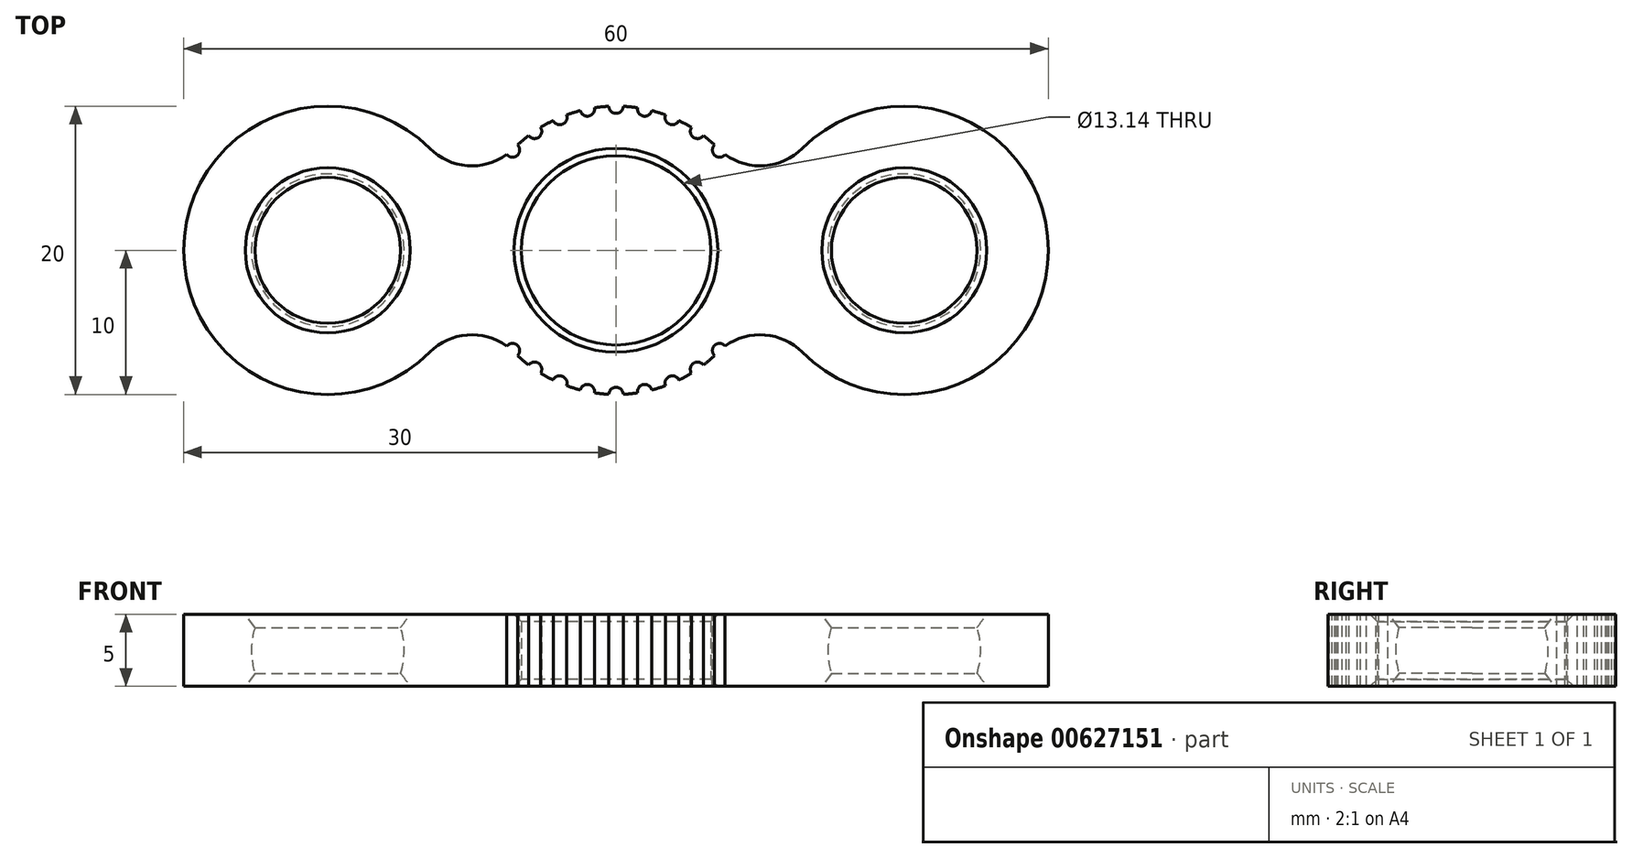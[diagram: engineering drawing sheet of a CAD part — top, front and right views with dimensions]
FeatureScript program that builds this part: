
annotation { "Feature Type Name" : "Feature", "Feature Type Description" : "" }
export const myFeature = defineFeature(function(context is Context, id is Id, definition is map)
    precondition{}
    {
        {
            var Q0;
            Q0=qCreatedBy(makeId("Top.planeOp"),FACE);
            var sketch = newSketch(context, id + "F0", { "sketchPlane" : qUnion([Q0])});
            skArc(sketch, "E0", {"start": v(-7.07, -7.07) * mm, "mid": v(0, -10) * mm, "end": v(7.07, -7.07) * mm});
            skArc(sketch, "E1", {"start": v(12.93, -7.07) * mm, "mid": v(30, 0) * mm, "end": v(12.93, 7.07) * mm});
            skArc(sketch, "E2", {"start": v(-12.93, 7.07) * mm, "mid": v(-30, 0) * mm, "end": v(-12.93, -7.07) * mm});
            skArc(sketch, "E3", {"start": v(7.07, 7.07) * mm, "mid": v(10, 5.86) * mm, "end": v(12.93, 7.07) * mm});
            skArc(sketch, "E4", {"start": v(-12.93, 7.07) * mm, "mid": v(-10, 5.86) * mm, "end": v(-7.07, 7.07) * mm});
            skArc(sketch, "E5.trimOffspring", {"start": v(7.07, 7.07) * mm, "mid": v(0, 10) * mm, "end": v(-7.07, 7.07) * mm});
            skArc(sketch, "E6", {"start": v(-7.07, -7.07) * mm, "mid": v(-10, -5.86) * mm, "end": v(-12.93, -7.07) * mm});
            skArc(sketch, "E7", {"start": v(12.93, -7.07) * mm, "mid": v(10, -5.86) * mm, "end": v(7.07, -7.07) * mm});
            skCircle(sketch, "E8", {"center": v(0, 0) * mm, "radius": 6.57 * mm});
            skSolve(sketch);
        }
        {
            var Q0;
            Q0=makeQuery(id+"F0.imprint","IMPRINT",FACE,{"disambiguationData":[TD([[makeQuery(id+"F0.imprint","IMPRINT",EDGE,{"derivedFrom":sQuery(id+"F0.wireOp",EDGE,"E0")}),1.0]])]});
            extrude(context, id + "F1", {"entities" : qUnion([Q0]), "depth" : 2.5 * mm, "offsetDistance" : 25 * mm});
        }
        {
            var Q0;
            Q0=makeQuery(id+"F1.opExtrude","CAP_FACE",FACE,{"disambiguationData":[OSD([sQuery(id+"F0.wireOp",EDGE,"E0"),sQuery(id+"F0.wireOp",EDGE,"E1"),sQuery(id+"F0.wireOp",EDGE,"E2"),sQuery(id+"F0.wireOp",EDGE,"E3"),sQuery(id+"F0.wireOp",EDGE,"E4"),sQuery(id+"F0.wireOp",EDGE,"E5.trimOffspring"),sQuery(id+"F0.wireOp",EDGE,"E6"),sQuery(id+"F0.wireOp",EDGE,"E7"),sQuery(id+"F0.wireOp",EDGE,"E8")])],"isStart":true});
            extrude(context, id + "F2", {"entities" : qUnion([Q0]), "operationType" : NewBodyOperationType.ADD, "depth" : 2.5 * mm, "offsetDistance" : 25 * mm});
        }
        {
            var Q0;
            Q0=qCreatedBy(makeId("Front.planeOp"),FACE);
            var sketch = newSketch(context, id + "F3", { "sketchPlane" : qUnion([Q0])});
            skArc(sketch, "E9", {"start": v(-20, 5.3) * mm, "mid": v(-25.3, 0) * mm, "end": v(-20, -5.3) * mm});
            skLineSegment(sketch, "E10", {"start": v(-20, 5.3) * mm, "end": v(-20, -5.3) * mm});
            skSolve(sketch);
        }
        {
            var Q0;
            Q0 = qSketchRegion(id + "F3", true);
            var Q1;
            Q1=sQuery(id+"F3.wireOp",EDGE,"E10");
            revolve(context, id + "F4", {"operationType" : NewBodyOperationType.REMOVE, "entities" : qUnion([Q0]), "axis" : qUnion([Q1]), "revolveType" : RevolveType.FULL, "oppositeDirection" : true, "surfaceOperationType" : NewSurfaceOperationType.NEW});
        }
        {
            var Q0;
            Q0=qCreatedBy(makeId("Front.planeOp"),FACE);
            var sketch = newSketch(context, id + "F5", { "sketchPlane" : qUnion([Q0])});
            skArc(sketch, "E11", {"start": v(20, -5.3) * mm, "mid": v(25.3, 0) * mm, "end": v(20, 5.3) * mm});
            skLineSegment(sketch, "E12", {"start": v(20, 5.3) * mm, "end": v(20, -5.3) * mm});
            skPoint(sketch, "E13.orphan", {"position": v(20, 9.13) * mm});
            skSolve(sketch);
        }
        {
            var Q0;
            Q0=makeQuery(id+"F5.imprint","IMPRINT",FACE,{"disambiguationData":[TD([[makeQuery(id+"F5.imprint","IMPRINT",EDGE,{"derivedFrom":sQuery(id+"F5.wireOp",EDGE,"E11")}),1.0]])]});
            var Q1;
            Q1=sQuery(id+"F5.wireOp",EDGE,"E12");
            revolve(context, id + "F6", {"operationType" : NewBodyOperationType.REMOVE, "entities" : qUnion([Q0]), "axis" : qUnion([Q1]), "revolveType" : RevolveType.FULL, "oppositeDirection" : true});
        }
        {
            var Q0;
            {var subQ0=sQuery(id+"F0.wireOp",EDGE,"E8");Q0=makeQuery(id+"F2.boolean.opBoolean","MERGE",FACE,{"derivedFrom":[makeQuery(id+"F1.opExtrude","SWEPT_FACE",FACE,{"disambiguationData":[OSD([subQ0])]}),makeQuery(id+"F2.opExtrude","SWEPT_FACE",FACE,{"disambiguationData":[OSD([subQ0])]})]});}
            chamfer(context, id + "F7", {"entities" : qUnion([Q0]), "width" : 0.5 * mm, "tangentPropagation" : true});
        }
        {
            var Q0;
            Q0=makeQuery(id+"F1.opExtrude","CAP_FACE",FACE,{"disambiguationData":[OSD([sQuery(id+"F0.wireOp",EDGE,"E0"),sQuery(id+"F0.wireOp",EDGE,"E1"),sQuery(id+"F0.wireOp",EDGE,"E2"),sQuery(id+"F0.wireOp",EDGE,"E3"),sQuery(id+"F0.wireOp",EDGE,"E4"),sQuery(id+"F0.wireOp",EDGE,"E5.trimOffspring"),sQuery(id+"F0.wireOp",EDGE,"E6"),sQuery(id+"F0.wireOp",EDGE,"E7"),sQuery(id+"F0.wireOp",EDGE,"E8")])],"isStart":false});
            var sketch = newSketch(context, id + "F8", { "sketchPlane" : qUnion([Q0])});
            skCircle(sketch, "E14", {"center": v(0, 10) * mm, "radius": 0.5 * mm});
            skCircle(sketch, "E15", {"center": v(1.99, 9.8) * mm, "radius": 0.5 * mm});
            skCircle(sketch, "E16", {"center": v(3.9, 9.2) * mm, "radius": 0.5 * mm});
            skCircle(sketch, "E17", {"center": v(5.65, 8.25) * mm, "radius": 0.5 * mm});
            skCircle(sketch, "E18", {"center": v(7.18, 6.96) * mm, "radius": 0.5 * mm});
            skCircle(sketch, "E19.MirrorC", {"center": v(-1.99, 9.8) * mm, "radius": 0.5 * mm});
            skCircle(sketch, "E20.MirrorC", {"center": v(-3.9, 9.2) * mm, "radius": 0.5 * mm});
            skCircle(sketch, "E21.MirrorC", {"center": v(-5.65, 8.25) * mm, "radius": 0.5 * mm});
            skCircle(sketch, "E22.MirrorC", {"center": v(-7.18, 6.96) * mm, "radius": 0.5 * mm});
            skCircle(sketch, "E23.MirrorC", {"center": v(7.18, -6.96) * mm, "radius": 0.5 * mm});
            skCircle(sketch, "E24.MirrorC", {"center": v(-7.18, -6.96) * mm, "radius": 0.5 * mm});
            skCircle(sketch, "E25.MirrorC", {"center": v(5.65, -8.25) * mm, "radius": 0.5 * mm});
            skCircle(sketch, "E26.MirrorC", {"center": v(-5.65, -8.25) * mm, "radius": 0.5 * mm});
            skCircle(sketch, "E27.MirrorC", {"center": v(-3.9, -9.2) * mm, "radius": 0.5 * mm});
            skCircle(sketch, "E28.MirrorC", {"center": v(1.99, -9.8) * mm, "radius": 0.5 * mm});
            skCircle(sketch, "E29.MirrorC", {"center": v(-1.99, -9.8) * mm, "radius": 0.5 * mm});
            skCircle(sketch, "E30.MirrorC", {"center": v(0, -10) * mm, "radius": 0.5 * mm});
            skCircle(sketch, "E31.MirrorC", {"center": v(3.9, -9.2) * mm, "radius": 0.5 * mm});
            skSolve(sketch);
        }
        {
            var Q0;
            Q0 = qSketchRegion(id + "F8", true);
            extrude(context, id + "F9", {"entities" : qUnion([Q0]), "operationType" : NewBodyOperationType.REMOVE, "oppositeDirection" : true, "depth" : 25 * mm, "offsetDistance" : 25 * mm});
        }
        {
            var Q0;
            Q0=makeQuery(id+"F6.boolean.opBoolean","INTERSECT",EDGE,{"derivedFrom":[makeQuery(id+"F1.opExtrude","CAP_FACE",FACE,{"disambiguationData":[OSD([sQuery(id+"F0.wireOp",EDGE,"E0"),sQuery(id+"F0.wireOp",EDGE,"E1"),sQuery(id+"F0.wireOp",EDGE,"E2"),sQuery(id+"F0.wireOp",EDGE,"E3"),sQuery(id+"F0.wireOp",EDGE,"E4"),sQuery(id+"F0.wireOp",EDGE,"E5.trimOffspring"),sQuery(id+"F0.wireOp",EDGE,"E6"),sQuery(id+"F0.wireOp",EDGE,"E7"),sQuery(id+"F0.wireOp",EDGE,"E8")])],"isStart":false}),makeQuery(id+"F6.opRevolve","SWEPT_FACE",FACE,{"disambiguationData":[OSD([sQuery(id+"F5.wireOp",EDGE,"E11")])]})]});
            var Q1;
            Q1=makeQuery(id+"F6.boolean.opBoolean","INTERSECT",EDGE,{"derivedFrom":[makeQuery(id+"F2.opExtrude","CAP_FACE",FACE,{"disambiguationData":[OSD([sQuery(id+"F0.wireOp",EDGE,"E0"),sQuery(id+"F0.wireOp",EDGE,"E1"),sQuery(id+"F0.wireOp",EDGE,"E2"),sQuery(id+"F0.wireOp",EDGE,"E3"),sQuery(id+"F0.wireOp",EDGE,"E4"),sQuery(id+"F0.wireOp",EDGE,"E5.trimOffspring"),sQuery(id+"F0.wireOp",EDGE,"E6"),sQuery(id+"F0.wireOp",EDGE,"E7"),sQuery(id+"F0.wireOp",EDGE,"E8")])],"isStart":false}),makeQuery(id+"F6.opRevolve","SWEPT_FACE",FACE,{"disambiguationData":[OSD([sQuery(id+"F5.wireOp",EDGE,"E11")])]})]});
            var Q2;
            Q2=makeQuery(id+"F4.boolean.opBoolean","INTERSECT",EDGE,{"derivedFrom":[makeQuery(id+"F1.opExtrude","CAP_FACE",FACE,{"disambiguationData":[OSD([sQuery(id+"F0.wireOp",EDGE,"E0"),sQuery(id+"F0.wireOp",EDGE,"E1"),sQuery(id+"F0.wireOp",EDGE,"E2"),sQuery(id+"F0.wireOp",EDGE,"E3"),sQuery(id+"F0.wireOp",EDGE,"E4"),sQuery(id+"F0.wireOp",EDGE,"E5.trimOffspring"),sQuery(id+"F0.wireOp",EDGE,"E6"),sQuery(id+"F0.wireOp",EDGE,"E7"),sQuery(id+"F0.wireOp",EDGE,"E8")])],"isStart":false}),makeQuery(id+"F4.opRevolve","SWEPT_FACE",FACE,{"disambiguationData":[OSD([sQuery(id+"F3.wireOp",EDGE,"E9")])]})]});
            var Q3;
            Q3=makeQuery(id+"F4.boolean.opBoolean","INTERSECT",EDGE,{"derivedFrom":[makeQuery(id+"F2.opExtrude","CAP_FACE",FACE,{"disambiguationData":[OSD([sQuery(id+"F0.wireOp",EDGE,"E0"),sQuery(id+"F0.wireOp",EDGE,"E1"),sQuery(id+"F0.wireOp",EDGE,"E2"),sQuery(id+"F0.wireOp",EDGE,"E3"),sQuery(id+"F0.wireOp",EDGE,"E4"),sQuery(id+"F0.wireOp",EDGE,"E5.trimOffspring"),sQuery(id+"F0.wireOp",EDGE,"E6"),sQuery(id+"F0.wireOp",EDGE,"E7"),sQuery(id+"F0.wireOp",EDGE,"E8")])],"isStart":false}),makeQuery(id+"F4.opRevolve","SWEPT_FACE",FACE,{"disambiguationData":[OSD([sQuery(id+"F3.wireOp",EDGE,"E9")])]})]});
            chamfer(context, id + "F10", {"entities" : qUnion([Q0, Q1, Q2, Q3]), "width" : 0.7 * mm, "tangentPropagation" : true});
        }
    });
